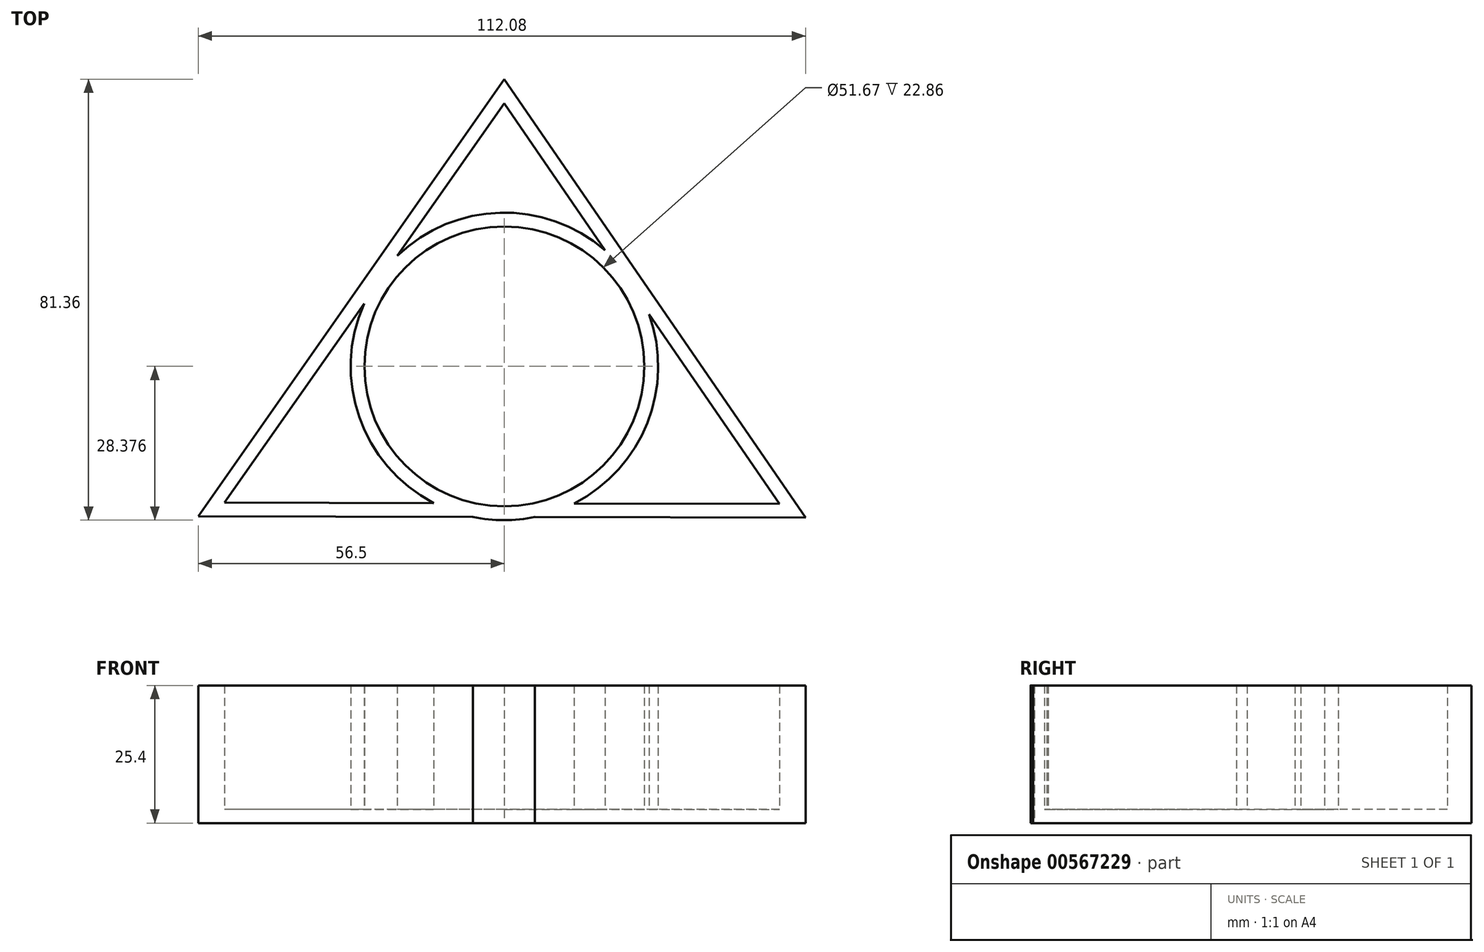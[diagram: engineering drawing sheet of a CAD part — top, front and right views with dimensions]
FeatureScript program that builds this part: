
annotation { "Feature Type Name" : "Feature", "Feature Type Description" : "" }
export const myFeature = defineFeature(function(context is Context, id is Id, definition is map)
    precondition{}
    {
        {
            var Q0;
            Q0=qCreatedBy(makeId("Top.planeOp"),FACE);
            var sketch = newSketch(context, id + "F0", { "sketchPlane" : qUnion([Q0])});
            skLineSegment(sketch, "E0", {"start": v(0, 55.58) * mm, "end": v(-56.5, -25.04) * mm});
            skLineSegment(sketch, "E1", {"start": v(0, 55.58) * mm, "end": v(55.58, -25.35) * mm});
            skLineSegment(sketch, "E2", {"start": v(55.58, -25.35) * mm, "end": v(-56.5, -25.04) * mm});
            skSolve(sketch);
        }
        {
            var Q0;
            Q0 = qSketchRegion(id + "F0", true);
            extrude(context, id + "F1", {"entities" : qUnion([Q0]), "depth" : 25.4 * mm, "offsetDistance" : 25.4 * mm});
        }
        {
            var Q0;
            Q0=makeQuery(id+"F1.opExtrude","CAP_FACE",FACE,{"disambiguationData":[OSD([sQuery(id+"F0.wireOp",EDGE,"E0"),sQuery(id+"F0.wireOp",EDGE,"E1"),sQuery(id+"F0.wireOp",EDGE,"E2")])],"isStart":false});
            shell(context, id + "F2", {"entities" : qUnion([Q0]), "thickness" : 2.54 * mm});
        }
        {
            var Q0;
            Q0=qCreatedBy(makeId("Top.planeOp"),FACE);
            var sketch = newSketch(context, id + "F3", { "sketchPlane" : qUnion([Q0])});
            skPoint(sketch, "E3", {"position": v(0, 2.6) * mm});
            skCircle(sketch, "E4", {"center": v(0, 2.6) * mm, "radius": 28.38 * mm});
            skSolve(sketch);
        }
        {
            var Q0;
            Q0 = qSketchRegion(id + "F3", true);
            extrude(context, id + "F4", {"entities" : qUnion([Q0]), "operationType" : NewBodyOperationType.ADD, "depth" : 25.4 * mm, "offsetDistance" : 25.4 * mm});
        }
        {
            var Q0;
            Q0=makeQuery(id+"F4.boolean.opBoolean","MERGE",FACE,{"derivedFrom":[makeQuery(id+"F1.opExtrude","CAP_FACE",FACE,{"disambiguationData":[OSD([sQuery(id+"F0.wireOp",EDGE,"E0"),sQuery(id+"F0.wireOp",EDGE,"E1"),sQuery(id+"F0.wireOp",EDGE,"E2")])],"isStart":false}),makeQuery(id+"F4.opExtrude","CAP_FACE",FACE,{"disambiguationData":[OSD([sQuery(id+"F3.wireOp",EDGE,"E4")])],"isStart":false})]});
            shell(context, id + "F5", {"entities" : qUnion([Q0]), "thickness" : 2.54 * mm});
        }
    });
